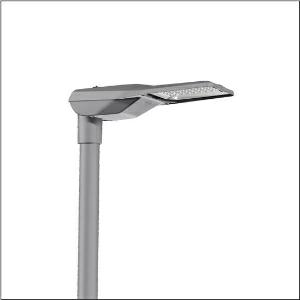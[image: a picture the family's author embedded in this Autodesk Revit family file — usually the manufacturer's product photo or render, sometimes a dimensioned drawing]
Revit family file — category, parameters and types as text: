
# Revit family: streetlight_sl_21_iq_mini___st1_0ab_5xe2m31v08jb_8772
name_source: partatom
category: Lighting Fixtures
units: mm (PartAtom-declared; Revit-internal decimal feet)

## family parameters
Cut with Voids When Loaded = No
Host = Face
Light Source = No
Part Type = Normal
Room Calculation Point = No
Round Connector Dimension = Use Diameter
Shared = No

## types (1)
- --- (1 x LED, 9870 lm, 72.5 W, 3000K)
    Apparent Load = 73 VA
    CIE Flux Codes = 40 74 97 100 100
    Color Rendering = 70
    Color Temperature = 3000K
    Default Elevation = 1800 mm
    Description = Streetlight SL 21 iQ mini, mast luminaire, primary light control with lens, of PMMA, primary optical cover: cover, of toughened safety glass, transparent, light distribution: ST1.0aB, light emission: direct distribution, primary light characteristic: asymmetric, installation type: post-top, side-entry, LED, High Power LED, rated luminous flux: 9.870lm, luminous efficacy: 136lm/W, light colour: 730, colour temperature: 3000K, control: presetting dimming logarithmic, Street-Remote, Auto-Match, Temp-Guard, Lumen-Switch, Night-Set, Smart-Wire, Light-Fading, Desk-Remote (wireless, voltage-free reading and setting of iQ features in the workshop via application-optimized NFC function/RFID function), optimised constant luminous flux control (CLO 2.0), mains connection: 220..240V, AC, 50/60Hz, start of lifetime: 73W, end of service life: 76W, reduction: 33W, luminaire housing, of diecast aluminium, powder-coated, Siteco® metallic grey (DB 702S), corrosivity category C5 mid according to DIN EN ISO 12944, please order mast flange separately, inclination adjustable: 0°, 5°, 10°, 15°, sealing non-destructively replaceable, multi-level sealing system, length: 628mm, width: 235mm, height: 110mm, mast flange for spigot size: 42mm (side-entry): 5XC10008XM4, 60/48mm (side-entry/post-top): 5XC10108XM2, 76/60mm (side-entry/post-top): 5XC10108XM1, Smart Interface above, protection rating (complete): IP66, insulation class (complete): insulation class II (safety insulation), certification: CE, ENEC, ENEC+, VDE, impact resistance: IK09, permissible operating ambient temperature for outdoor applications: -40..+50°C, standard-compliant lighting for roads and squares, packaging unit: 1 piece

Light Distribution: ST1.0aB
    Height = 110 mm
    Lamp = 1 x LED
    Lamp Light Flux = 9870 lm
    Lamp Power = 72.5 W
    Lamp count = 1
    Length = 625 mm
    Luminous efficacy = 136 lm/W
    Manufacturer = Siteco
    ModVariant = No
    Model = 5XE2M31V08JB
    Number of Poles = 1
    OnlyDefault = Yes
    Power Factor = 1
    Product Name = Streetlight SL 21 iQ mini | ST1.0aB
    Product group = mast luminaire | pylon top
    ProductGroupID = 6100
    Protection Class = Protection class II
    Protection Degree = IP 66
    RLX_Detail_Level = 1
    RLX_Emergency_Light_Flux = 0 lm
    RLX_Emergency_Type = 0
    RLX_Emergency_Type_DB = No
    RlxData = <blob elided: 92429 chars, md5=ac2f2605>
    Socket = socket
    Standby Power = 0 W
    System Light Flux = 9870 lm
    System Power = 73 W
    Type Comments = factory setting: luminous flux: 100 % | dim-lin: 254 | 755 mA
    Type Image = l_1003515.jpg
    URL = http://relux.com
    VarID = @adj_060451
    Voltage = 0 V
    Weight = 0.00 kg
    Width = 234 mm

## geometry (parser evidence)
native form markers: Blend x4, Sweep x11
no freeform markers — native parametric forms only
